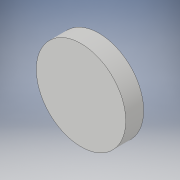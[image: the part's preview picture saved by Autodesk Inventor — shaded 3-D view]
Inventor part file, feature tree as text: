
AUTODESK INVENTOR PART (.ipt)
format: ipt  version: 2019 (Build 230136000, 136)  size: 91,136 bytes
history: native  units: mm
features: other x1, extrude x1, sketch x1
ambient origin geometry x8: Origin, YZ Plane, XZ Plane, XY Plane, X Axis, Y Axis, Z Axis, Center Point
bodies: Body1 (feature_tree)
feature tree (3):
  other  "Твердое тело1"
  extrude  "Выдавливание1"  Depth=50.0mm
  sketch  "Эскиз1"
